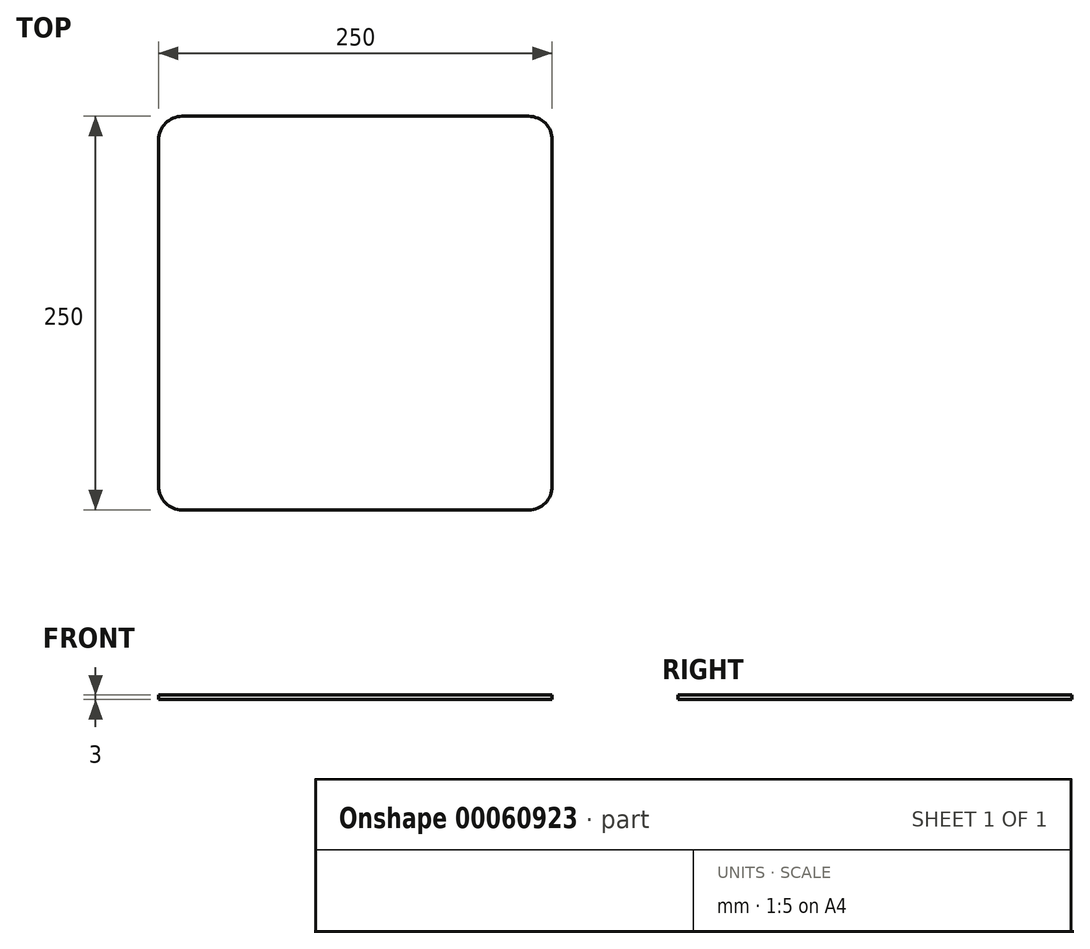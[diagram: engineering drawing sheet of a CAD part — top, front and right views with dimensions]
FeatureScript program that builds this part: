
annotation { "Feature Type Name" : "Feature", "Feature Type Description" : "" }
export const myFeature = defineFeature(function(context is Context, id is Id, definition is map)
    precondition{}
    {
        {
            var Q0;
            Q0=qCreatedBy(makeId("Top.planeOp"),FACE);
            var sketch = newSketch(context, id + "F0", { "sketchPlane" : qUnion([Q0])});
            skLineSegment(sketch, "E0.rect.bottom", {"start": v(-110, 125) * mm, "end": v(110, 125) * mm});
            skLineSegment(sketch, "E0.rect.top", {"start": v(-110, -125) * mm, "end": v(110, -125) * mm});
            skLineSegment(sketch, "E0.rect.left", {"start": v(-125, 110) * mm, "end": v(-125, -110) * mm});
            skLineSegment(sketch, "E0.rect.right", {"start": v(125, 110) * mm, "end": v(125, -110) * mm});
            skPoint(sketch, "E0.rect.middle", {"position": v(0, 0) * mm});
            skPoint(sketch, "E1.visualSharp", {"position": v(-125, -125) * mm});
            skArc(sketch, "E1.filletArc", {"start": v(-125, -110) * mm, "mid": v(-120.6, -120.6) * mm, "end": v(-110, -125) * mm});
            skPoint(sketch, "E2.visualSharp", {"position": v(125, -125) * mm});
            skArc(sketch, "E2.filletArc", {"start": v(110, -125) * mm, "mid": v(120.6, -120.6) * mm, "end": v(125, -110) * mm});
            skPoint(sketch, "E3.visualSharp", {"position": v(125, 125) * mm});
            skArc(sketch, "E3.filletArc", {"start": v(125, 110) * mm, "mid": v(120.6, 120.6) * mm, "end": v(110, 125) * mm});
            skPoint(sketch, "E4.visualSharp", {"position": v(-125, 125) * mm});
            skArc(sketch, "E4.filletArc", {"start": v(-110, 125) * mm, "mid": v(-120.6, 120.6) * mm, "end": v(-125, 110) * mm});
            skSolve(sketch);
        }
        {
            var Q0;
            Q0=makeQuery(id+"F0.imprint","IMPRINT",FACE,{"disambiguationData":[TD([[makeQuery(id+"F0.imprint","IMPRINT",EDGE,{"derivedFrom":sQuery(id+"F0.wireOp",EDGE,"E0.rect.bottom")}),-1.0]])]});
            extrude(context, id + "F1", {"entities" : qUnion([Q0]), "depth" : 3 * mm});
        }
    });
